# Revit family: Haworth_Planes_ColumnBaseConferenceTable_Round
name_source: partatom
category: Furniture Systems
revit_build: Autodesk Revit 2018 (Build: 20170223_1515(x64)
units: mm (PartAtom-declared; Revit-internal decimal feet)

## family parameters
Always vertical = Yes
Cut with Voids When Loaded = No
OmniClass Number = 23.40.70.14.64.21
OmniClass Title = Systems Furniture
Part Type = Normal
Room Calculation Point = No
Round Connector Dimension = Use Diameter
Shared = No
Work Plane-Based = No

## types (5) — shared parameters
Actual Height = 29"
Assembly Code = E2020200
Base Finish = Haworth _ Paint _ Graphite
Custom Size = No
Cutout = Yes
Cutout Depth = 4"
Cutout Width = 11"
Edgeband = Yes
Flip Top = Yes
Flip Top Finish = Haworth _ Paint _ Metallic Champagne
Fliptop Depth = 4 3/8"
Fliptop Width = 11 1/4"
Frame Finish = Haworth _ Paint _ Graphite
Height = 29"
Knife Edge = No
Manufacturer = Haworth
Max. Depth = 60"
Max. Height = 41 1/4"
Max. Width = 60"
Min. Depth = 36"
Min. Height = 21 1/4"
Min. Width = 36"
Model = TARQ
Opening Double = No
Opening Double Wide = No
Opening Single = No
Opening Single Wide = Yes
Revision Number = 1
Size = Verify Final Dim. w/ Haworth
Standard Depths = 36, 42, 48, 54, 60 in.
Standard Heights = 21.25, 29, 41.25 in.
Standard Widths = 36, 42, 48, 54, 60 in.
Support Height = 27 13/16"
Sustainability Info = https://www.haworth.com
Table Thickness = 1 3/16"
URL = www.haworth.com
URL - Product = https://www.haworth.com
Warranty = https://www.haworth.com

## per-type parameters (varying)
| type | Actual Depth | Actual Width | Depth | Description | Large Base | Width |
| 60d 60w 29h | 60" | 60" | 60" | Haworth - Planes Column Base - Round - 60w 60d 29h | Yes | 60" |
| 54d 54w 29h | 54" | 54" | 54" | Haworth - Planes Column Base - Round - 54w 54d 29h | Yes | 54" |
| 48d 48w 29h | 48" | 48" | 48" | Haworth - Planes Column Base - Round - 48w 48d 29h | Yes | 48" |
| 42d 42w 29h | 42" | 42" | 42" | Haworth - Planes Column Base - Round - 42w 42d 29h | Yes | 42" |
| 36d 36w 29h | 36" | 36" | 36" | Haworth - Planes Column Base - Round - 36w 36d 29h | No | 36" |

## geometry (parser evidence)
native form markers: Sweep x11
no freeform markers — native parametric forms only
